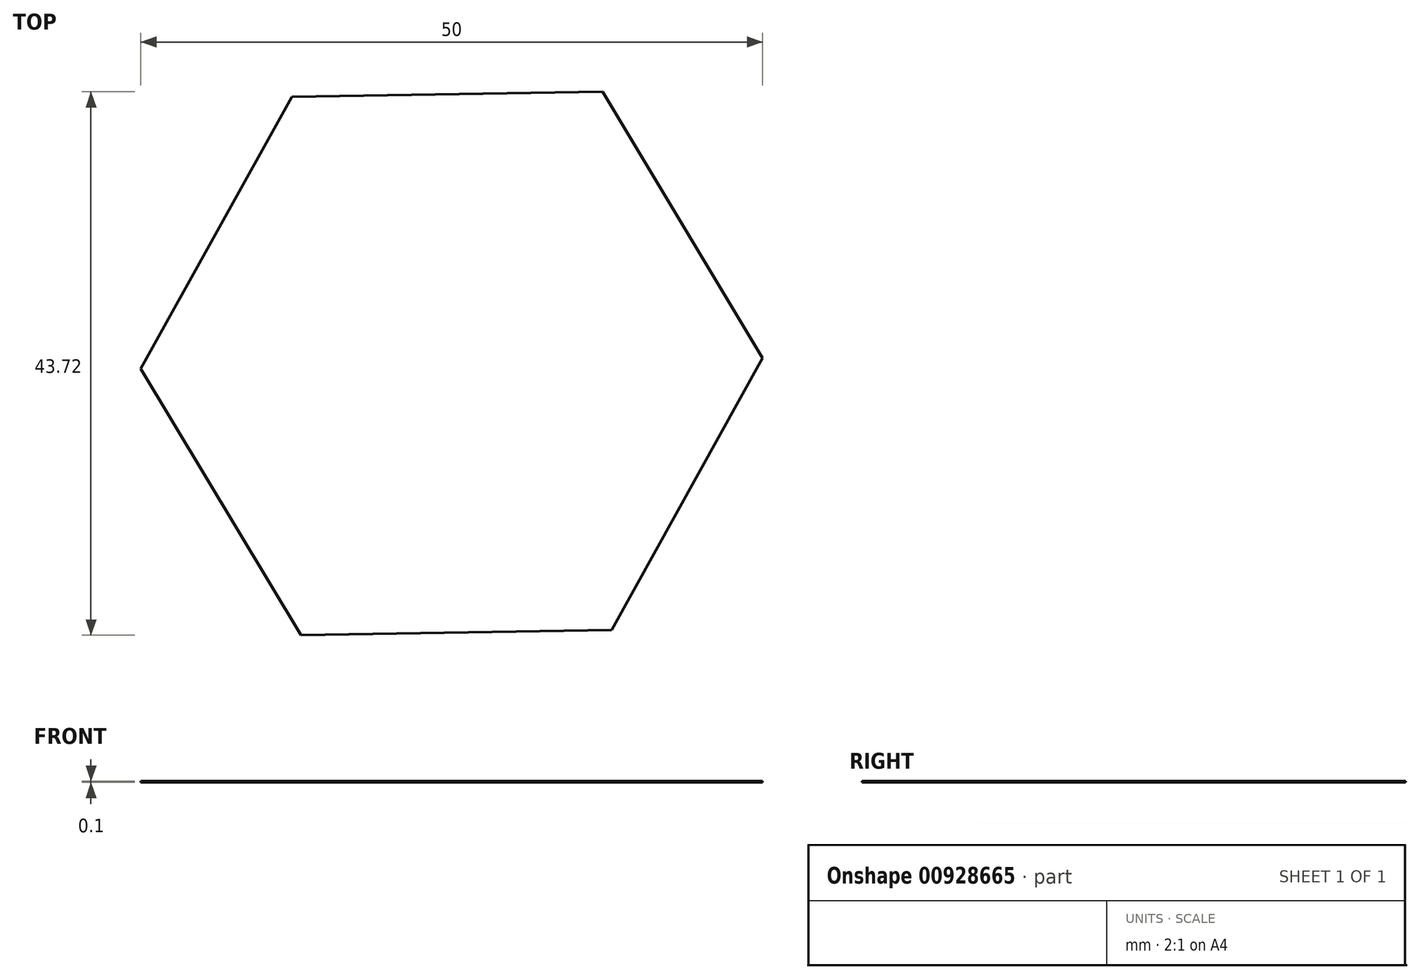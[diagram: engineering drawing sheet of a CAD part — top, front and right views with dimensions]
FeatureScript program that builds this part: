
annotation { "Feature Type Name" : "Feature", "Feature Type Description" : "" }
export const myFeature = defineFeature(function(context is Context, id is Id, definition is map)
    precondition{}
    {
        {
            var Q0;
            Q0=qCreatedBy(makeId("Top.planeOp"),FACE);
            var sketch = newSketch(context, id + "F0", { "sketchPlane" : qUnion([Q0])});
            skCircle(sketch, "E0.cCircle", {"center": v(0, 0) * mm, "radius": 21.65 * mm, "construction": true});
            skLineSegment(sketch, "E0.0", {"start": v(25, 0.42) * mm, "end": v(12.86, -21.44) * mm});
            skLineSegment(sketch, "E0.1", {"start": v(12.86, -21.44) * mm, "end": v(-12.13, -21.86) * mm});
            skLineSegment(sketch, "E0.2", {"start": v(-12.13, -21.86) * mm, "end": v(-25, -0.42) * mm});
            skLineSegment(sketch, "E0.3", {"start": v(-25, -0.42) * mm, "end": v(-12.86, 21.44) * mm});
            skLineSegment(sketch, "E0.4", {"start": v(-12.86, 21.44) * mm, "end": v(12.13, 21.86) * mm});
            skLineSegment(sketch, "E0.5", {"start": v(12.13, 21.86) * mm, "end": v(25, 0.42) * mm});
            skPoint(sketch, "E0.0.midPoint", {"position": v(18.93, -10.5) * mm});
            skSolve(sketch);
        }
        {
            var Q0;
            Q0=makeQuery(id+"F0.imprint","IMPRINT",FACE,{"disambiguationData":[TD([[makeQuery(id+"F0.imprint","IMPRINT",EDGE,{"derivedFrom":sQuery(id+"F0.wireOp",EDGE,"E0.0")}),-1.0]])]});
            extrude(context, id + "F1", {"entities" : qUnion([Q0]), "depth" : 0.1 * mm, "offsetDistance" : 25 * mm});
        }
    });
